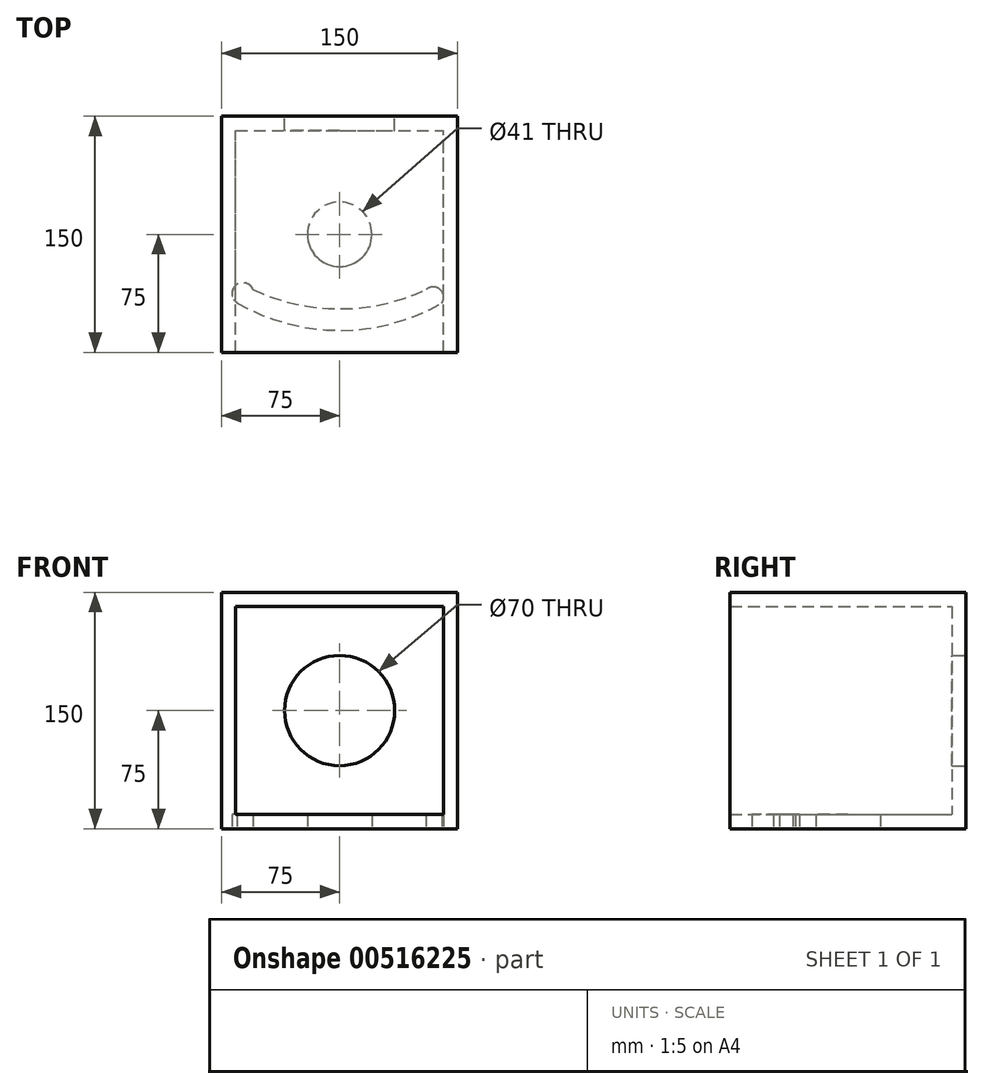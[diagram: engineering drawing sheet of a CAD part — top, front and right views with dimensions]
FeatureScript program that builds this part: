
annotation { "Feature Type Name" : "Feature", "Feature Type Description" : "" }
export const myFeature = defineFeature(function(context is Context, id is Id, definition is map)
    precondition{}
    {
        {
            var Q0;
            Q0=qCreatedBy(makeId("Front.planeOp"),FACE);
            var sketch = newSketch(context, id + "F0", { "sketchPlane" : qUnion([Q0])});
            skLineSegment(sketch, "E0.bottom", {"start": v(-75, 75) * mm, "end": v(75, 75) * mm});
            skLineSegment(sketch, "E0.top", {"start": v(-75, -75) * mm, "end": v(75, -75) * mm});
            skLineSegment(sketch, "E0.left", {"start": v(-75, 75) * mm, "end": v(-75, -75) * mm});
            skLineSegment(sketch, "E0.right", {"start": v(75, 75) * mm, "end": v(75, -75) * mm});
            skPoint(sketch, "E0.middle", {"position": v(0, 0) * mm});
            skSolve(sketch);
        }
        {
            var Q0;
            Q0=makeQuery(id+"F0.imprint","IMPRINT",FACE,{"disambiguationData":[TD([[makeQuery(id+"F0.imprint","IMPRINT",EDGE,{"derivedFrom":sQuery(id+"F0.wireOp",EDGE,"E0.bottom")}),-1.0]])]});
            extrude(context, id + "F1", {"entities" : qUnion([Q0]), "depth" : 9 * mm, "offsetDistance" : 25 * mm});
        }
        {
            var Q0;
            Q0=makeQuery(id+"F1.opExtrude","CAP_FACE",FACE,{"disambiguationData":[OSD([sQuery(id+"F0.wireOp",EDGE,"E0.bottom"),sQuery(id+"F0.wireOp",EDGE,"E0.top"),sQuery(id+"F0.wireOp",EDGE,"E0.left"),sQuery(id+"F0.wireOp",EDGE,"E0.right")])],"isStart":false});
            var sketch = newSketch(context, id + "F2", { "sketchPlane" : qUnion([Q0])});
            skLineSegment(sketch, "E1", {"start": v(-66, 66) * mm, "end": v(-66, -66) * mm});
            skLineSegment(sketch, "E2", {"start": v(66, 66) * mm, "end": v(66, -66) * mm});
            skLineSegment(sketch, "E3", {"start": v(-66, 66) * mm, "end": v(66, 66) * mm});
            skLineSegment(sketch, "E4", {"start": v(-66, -66) * mm, "end": v(66, -66) * mm});
            skSolve(sketch);
        }
        {
            var Q0;
            Q0=makeQuery(id+"F2.imprint","IMPRINT",FACE,{"disambiguationData":[TD([[makeQuery(id+"F2.imprint","IMPRINT",EDGE,{"derivedFrom":sQuery(id+"F2.wireOp",EDGE,"E1")}),-1.0]])]});
            extrude(context, id + "F3", {"entities" : qUnion([Q0]), "operationType" : NewBodyOperationType.ADD, "depth" : 141 * mm, "offsetDistance" : 25 * mm});
        }
        {
            var Q0;
            {var subQ0=sQuery(id+"F0.wireOp",EDGE,"E0.top");Q0=makeQuery(id+"F3.boolean.opBoolean","MERGE",FACE,{"derivedFrom":[makeQuery(id+"F1.opExtrude","SWEPT_FACE",FACE,{"disambiguationData":[OSD([subQ0])]}),makeQuery(id+"F3.opExtrude","SWEPT_FACE",FACE,{"disambiguationData":[OSD([subQ0])]})]});}
            var sketch = newSketch(context, id + "F4", { "sketchPlane" : qUnion([Q0])});
            skCircle(sketch, "E5", {"center": v(0, 75) * mm, "radius": 20.5 * mm});
            skPoint(sketch, "E6.trimOffspring.end.orphan", {"position": v(75, 75) * mm});
            skPoint(sketch, "E7.start.orphan", {"position": v(0, 150) * mm});
            skPoint(sketch, "E8.start.orphan", {"position": v(-75, 75) * mm});
            skPoint(sketch, "E9.trimOffspring.end.orphan", {"position": v(0, 0) * mm});
            skSolve(sketch);
        }
        {
            var Q0;
            Q0=makeQuery(id+"F4.imprint","IMPRINT",FACE,{"disambiguationData":[TD([[makeQuery(id+"F4.imprint","IMPRINT",EDGE,{"derivedFrom":sQuery(id+"F4.wireOp",EDGE,"E5")}),1.0]])]});
            extrude(context, id + "F5", {"entities" : qUnion([Q0]), "operationType" : NewBodyOperationType.REMOVE, "endBound" : BoundingType.UP_TO_NEXT, "oppositeDirection" : true, "depth" : 25 * mm, "offsetDistance" : 25 * mm});
        }
        {
            var Q0;
            Q0=makeQuery(id+"F1.opExtrude","CAP_FACE",FACE,{"disambiguationData":[OSD([sQuery(id+"F0.wireOp",EDGE,"E0.bottom"),sQuery(id+"F0.wireOp",EDGE,"E0.top"),sQuery(id+"F0.wireOp",EDGE,"E0.left"),sQuery(id+"F0.wireOp",EDGE,"E0.right")])],"isStart":true});
            var sketch = newSketch(context, id + "F6", { "sketchPlane" : qUnion([Q0])});
            skCircle(sketch, "E10", {"center": v(0, 0) * mm, "radius": 35 * mm});
            skSolve(sketch);
        }
        {
            var Q0;
            Q0=makeQuery(id+"F6.imprint","IMPRINT",FACE,{"disambiguationData":[TD([[makeQuery(id+"F6.imprint","IMPRINT",EDGE,{"derivedFrom":sQuery(id+"F6.wireOp",EDGE,"E10")}),1.0]])]});
            extrude(context, id + "F7", {"entities" : qUnion([Q0]), "operationType" : NewBodyOperationType.REMOVE, "endBound" : BoundingType.UP_TO_NEXT, "oppositeDirection" : true, "depth" : 25 * mm, "offsetDistance" : 25 * mm});
        }
        {
            var Q0;
            {var subQ0=sQuery(id+"F0.wireOp",EDGE,"E0.top");Q0=makeQuery(id+"F3.boolean.opBoolean","MERGE",FACE,{"derivedFrom":[makeQuery(id+"F1.opExtrude","SWEPT_FACE",FACE,{"disambiguationData":[OSD([subQ0])]}),makeQuery(id+"F3.opExtrude","SWEPT_FACE",FACE,{"disambiguationData":[OSD([subQ0])]})]});}
            var sketch = newSketch(context, id + "F8", { "sketchPlane" : qUnion([Q0])});
            skArc(sketch, "E11", {"start": v(65, 118.55) * mm, "mid": v(0, 136) * mm, "end": v(-65, 118.55) * mm});
            skArc(sketch, "E12", {"start": v(55, 110) * mm, "mid": v(0, 122.3) * mm, "end": v(-55, 110) * mm});
            skArc(sketch, "E13", {"start": v(55, 110) * mm, "mid": v(63.7, 109.95) * mm, "end": v(65, 118.55) * mm});
            skArc(sketch, "E14", {"start": v(-65, 118.55) * mm, "mid": v(-65.9, 107.37) * mm, "end": v(-55, 110) * mm});
            skSolve(sketch);
        }
        {
            var Q0;
            Q0=makeQuery(id+"F8.imprint","IMPRINT",FACE,{"disambiguationData":[TD([[makeQuery(id+"F8.imprint","IMPRINT",EDGE,{"derivedFrom":sQuery(id+"F8.wireOp",EDGE,"E11")}),1.0]])]});
            var Q1;
            Q1=makeQuery(id+"F3.opExtrude","SWEPT_FACE",FACE,{"disambiguationData":[OSD([sQuery(id+"F2.wireOp",EDGE,"E4")])]});
            extrude(context, id + "F9", {"entities" : qUnion([Q0]), "operationType" : NewBodyOperationType.REMOVE, "endBound" : BoundingType.UP_TO_SURFACE, "oppositeDirection" : true, "depth" : 25 * mm, "endBoundEntityFace" : qUnion([Q1]), "offsetDistance" : 25 * mm});
        }
    });
